# Revit family: KEUCO_14963010003
name_source: partatom
category: Sonderausstattung
revit_build: Autodesk Revit 2016 (Build: 20150220_1215(x64)
units: mm (PartAtom-declared; Revit-internal decimal feet)

## family parameters
Arbeitsebenenbasiert = Nein
Beim Laden mit Abzugskörper schneiden = Nein
Bemaßung runder Anschluss = Durchmesser verwenden
Gemeinsam genutzt = Nein
Immer vertikal = Ja
Raumberechnungspunkt = Nein
Teiletyp = Normal

## types (3) — shared parameters
Beschreibung = für Rollenbreite 100/120 mm
Gewicht = 382
Hersteller = KEUCO
Kategorie = ACC
Preisgruppe = 1
Serie = Plan
URL = https://www.keuco.com
Verwendung = GWC / WC

## per-type parameters (varying)
| type | Ausschreibungstext |
| 14963010003 | KEUCO PLAN Doppel-Toilettenpapierhalter, 14963010003
hochglanzverchromter Doppel-Toilettenpapierhalter für Rollenbreite 100/120 mm, 
mit integrierter Rollenbremse aus thermoplast. Elastomer-Kunststoff, 
in ästhetischem, funktionalem Design,
Breite: 298 mm, Gesamtausladung ohne WC Papierrolle: 65 mm, 
Rohrdurchmesser 22 mm,
der Doppel-Toilettenpapierhalter wird verdeckt angebracht,
Lieferung inkl. korrosionsfreiem Befestigungsmaterial |
| 14963070003 | KEUCO PLAN Doppel-Toilettenpapierhalter, 14963070003
Doppel-Toilettenpapierhalter aus hochwertigem Edelstahl,
für Rollenbreite 100/120 mm, 
mit integrierter Rollenbremse aus thermoplast. Elastomer-Kunststoff, 
in ästhetischem, funktionalem Design,
Breite: 298 mm, Gesamtausladung ohne WC Papierrolle: 65 mm, 
Rohrdurchmesser 22 mm,
der Doppel-Toilettenpapierhalter wird verdeckt angebracht,
Lieferung inkl. korrosionsfreiem Befestigungsmaterial |
| 14963170003 | KEUCO PLAN Doppel-Toilettenpapierhalter, 14963170003
Doppel-Toilettenpapierhalter aus silber-eloxiertem Aluminium (E6 EV1),
für Rollenbreite 100/120 mm, 
mit integrierter Rollenbremse aus thermoplast. Elastomer-Kunststoff, 
in ästhetischem, funktionalem Design,
Breite: 298 mm, Gesamtausladung ohne WC Papierrolle: 65 mm, 
Rohrdurchmesser 22 mm,
der Doppel-Toilettenpapierhalter wird verdeckt angebracht,
Lieferung inkl. korrosionsfreiem Befestigungsmaterial |

note: column(s) folded — value = type name in every type: Artikelnummer

## geometry (parser evidence)
native form markers: Blend x2, Sweep x3
no freeform markers — native parametric forms only
